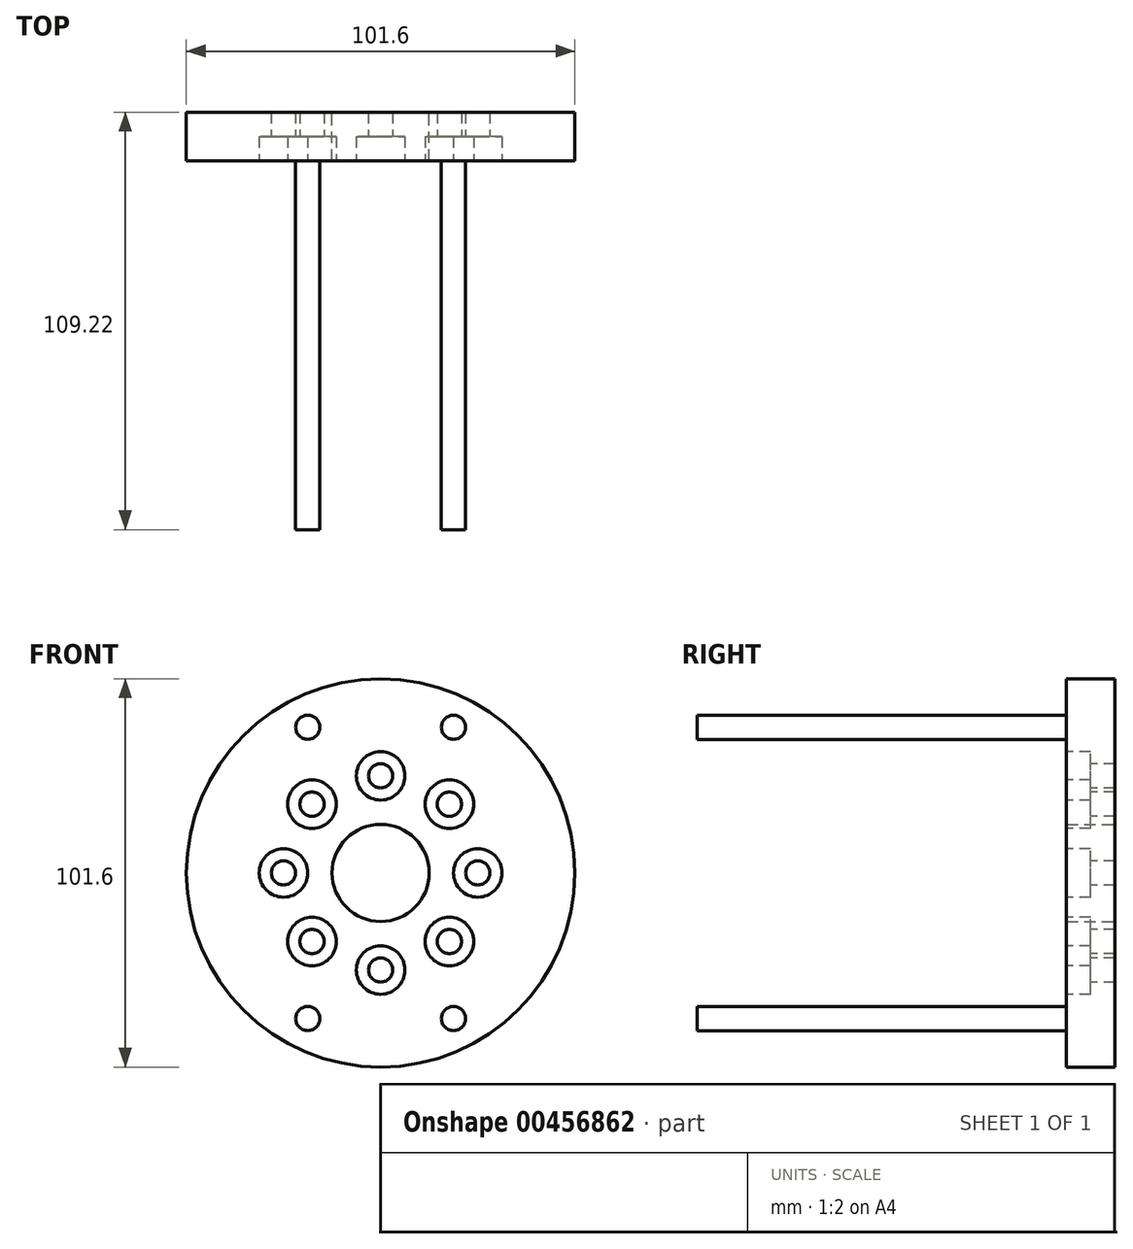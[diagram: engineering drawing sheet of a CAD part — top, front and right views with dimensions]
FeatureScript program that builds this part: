
annotation { "Feature Type Name" : "Feature", "Feature Type Description" : "" }
export const myFeature = defineFeature(function(context is Context, id is Id, definition is map)
    precondition{}
    {
        {
            var Q0;
            Q0=qCreatedBy(makeId("Front.planeOp"),FACE);
            var sketch = newSketch(context, id + "F0", { "sketchPlane" : qUnion([Q0])});
            skCircle(sketch, "E0", {"center": v(0, 0) * mm, "radius": 50.8 * mm});
            skCircle(sketch, "E1", {"center": v(0, 0) * mm, "radius": 12.7 * mm});
            skCircle(sketch, "E2", {"center": v(0, 0) * mm, "radius": 34.93 * mm, "construction": true});
            skPoint(sketch, "E3", {"position": v(0, 34.93) * mm});
            skPoint(sketch, "E4", {"position": v(-34.93, 0) * mm});
            skPoint(sketch, "E5", {"position": v(0, -34.92) * mm});
            skPoint(sketch, "E6", {"position": v(34.93, 0) * mm});
            skSolve(sketch);
        }
        {
            var Q0;
            Q0=qSketchRegion(id+"F0",true);
            extrude(context, id + "F1", {"entities" : qUnion([Q0]), "depth" : 12.7 * mm});
        }
        {
            var Q0;
            Q0=makeQuery(id+"F1.opExtrude","CAP_FACE",FACE,{"disambiguationData":[OSD([sQuery(id+"F0.wireOp",EDGE,"E0")])],"isStart":false});
            var sketch = newSketch(context, id + "F2", { "sketchPlane" : qUnion([Q0])});
            skCircle(sketch, "E7", {"center": v(-17.96, 17.96) * mm, "radius": 6.35 * mm});
            skCircle(sketch, "E8", {"center": v(17.96, 17.96) * mm, "radius": 6.35 * mm});
            skCircle(sketch, "E9", {"center": v(17.96, -17.96) * mm, "radius": 6.35 * mm});
            skCircle(sketch, "E10", {"center": v(-17.96, -17.96) * mm, "radius": 6.35 * mm});
            skCircle(sketch, "E11", {"center": v(0, 0) * mm, "radius": 25.4 * mm, "construction": true});
            skLineSegment(sketch, "E12", {"start": v(0, 0) * mm, "end": v(-17.96, 17.96) * mm, "construction": true});
            skLineSegment(sketch, "E13", {"start": v(0, 0) * mm, "end": v(-25.4, 0) * mm, "construction": true});
            skPoint(sketch, "E14", {"position": v(0, 25.4) * mm});
            skPoint(sketch, "E15", {"position": v(-25.4, 0) * mm});
            skPoint(sketch, "E16", {"position": v(25.4, 0) * mm});
            skPoint(sketch, "E17", {"position": v(0, -25.4) * mm});
            skSolve(sketch);
        }
        {
            var Q0;
            Q0=qSketchRegion(id+"F2",true);
            extrude(context, id + "F3", {"entities" : qUnion([Q0]), "operationType" : NewBodyOperationType.REMOVE, "oppositeDirection" : true, "depth" : 6.35 * mm});
        }
        {
            var Q0;
            Q0=sQuery(id+"F2.wireOp",VERTEX,"E14");
            var Q1;
            Q1=sQuery(id+"F2.wireOp",VERTEX,"E15");
            var Q2;
            Q2=sQuery(id+"F2.wireOp",VERTEX,"E17");
            var Q3;
            Q3=sQuery(id+"F2.wireOp",VERTEX,"E16");
            var Q4;
            Q4=makeQuery(id+"F1.opExtrude","SWEPT_BODY",BODY,{"disambiguationData":[OSD([sQuery(id+"F0.wireOp",EDGE,"E0"),sQuery(id+"F0.wireOp",EDGE,"E1")])]});
            hole(context, id + "F4", {"style" : HoleStyle.C_BORE, "holeDiameter" : 6.35 * mm, "cBoreDiameter" : 12.7 * mm, "cBoreDepth" : 6.35 * mm, "endStyle" : HoleEndStyle.THROUGH, "locations" : qUnion([Q0, Q1, Q2, Q3]), "scope" : qUnion([Q4])});
        }
        {
            var Q0;
            Q0=makeQuery(id+"F1.opExtrude","CAP_FACE",FACE,{"disambiguationData":[OSD([sQuery(id+"F0.wireOp",EDGE,"E0"),sQuery(id+"F0.wireOp",EDGE,"E1")])],"isStart":false});
            var sketch = newSketch(context, id + "F5", { "sketchPlane" : qUnion([Q0])});
            skCircle(sketch, "E18", {"center": v(-19.05, 38.1) * mm, "radius": 3.18 * mm});
            skCircle(sketch, "E19", {"center": v(19.05, 38.1) * mm, "radius": 3.18 * mm});
            skCircle(sketch, "E20", {"center": v(19.05, -38.1) * mm, "radius": 3.18 * mm});
            skCircle(sketch, "E21", {"center": v(-19.05, -38.1) * mm, "radius": 3.18 * mm});
            skLineSegment(sketch, "E22.bottom", {"start": v(-19.05, -38.1) * mm, "end": v(19.05, -38.1) * mm, "construction": true});
            skLineSegment(sketch, "E22.top", {"start": v(-19.05, 38.1) * mm, "end": v(19.05, 38.1) * mm, "construction": true});
            skLineSegment(sketch, "E22.left", {"start": v(-19.05, -38.1) * mm, "end": v(-19.05, 38.1) * mm, "construction": true});
            skLineSegment(sketch, "E22.right", {"start": v(19.05, -38.1) * mm, "end": v(19.05, 38.1) * mm, "construction": true});
            skSolve(sketch);
        }
        {
            var Q0;
            Q0=qSketchRegion(id+"F5",true);
            extrude(context, id + "F6", {"entities" : qUnion([Q0]), "operationType" : NewBodyOperationType.ADD, "depth" : 96.52 * mm});
        }
        {
            var Q0;
            Q0=makeQuery(id+"F3.boolean.opBoolean","COPY",FACE,{"derivedFrom":makeQuery(id+"F3.opExtrude","CAP_FACE",FACE,{"disambiguationData":[OSD([sQuery(id+"F2.wireOp",EDGE,"E7")])],"isStart":false})});
            var sketch = newSketch(context, id + "F7", { "sketchPlane" : qUnion([Q0])});
            skCircle(sketch, "E23", {"center": v(-17.96, 17.96) * mm, "radius": 3.18 * mm});
            skCircle(sketch, "E24.0.1.0", {"center": v(-17.96, -17.96) * mm, "radius": 3.18 * mm});
            skCircle(sketch, "E24.1.0.0", {"center": v(17.96, 17.96) * mm, "radius": 3.18 * mm});
            skCircle(sketch, "E24.1.1.0", {"center": v(17.96, -17.96) * mm, "radius": 3.18 * mm});
            skLineSegment(sketch, "E24.direction1", {"start": v(-17.96, 17.96) * mm, "end": v(17.96, 17.96) * mm, "construction": true});
            skLineSegment(sketch, "E24.direction2", {"start": v(-17.96, 17.96) * mm, "end": v(-17.96, -17.96) * mm, "construction": true});
            skSolve(sketch);
        }
        {
            var Q0;
            Q0=qSketchRegion(id+"F7",true);
            extrude(context, id + "F8", {"entities" : qUnion([Q0]), "operationType" : NewBodyOperationType.REMOVE, "oppositeDirection" : true, "depth" : 25.4 * mm});
        }
    });
